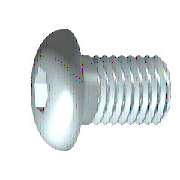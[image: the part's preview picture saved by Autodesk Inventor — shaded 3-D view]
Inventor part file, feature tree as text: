
AUTODESK INVENTOR PART (.ipt)
format: ipt  version: 2023.5 (Build 275446000, 446)  size: 198,144 bytes
history: native  units: mm (DEFAULTED — no unit token found)
features: extrude x1, plane x1, fillet x1
ambient origin geometry x7: Origin, YZ Plane, XY Plane, X Axis, Y Axis, Z Axis, Center Point
bodies: Solid1 (feature_tree), Body (feature_tree)
feature tree (3):
  extrude  "Slot"  Depth=7.366mm
  plane  "Work Plane1"
  fillet  "Fillet2"  Radius=2.116784mm
